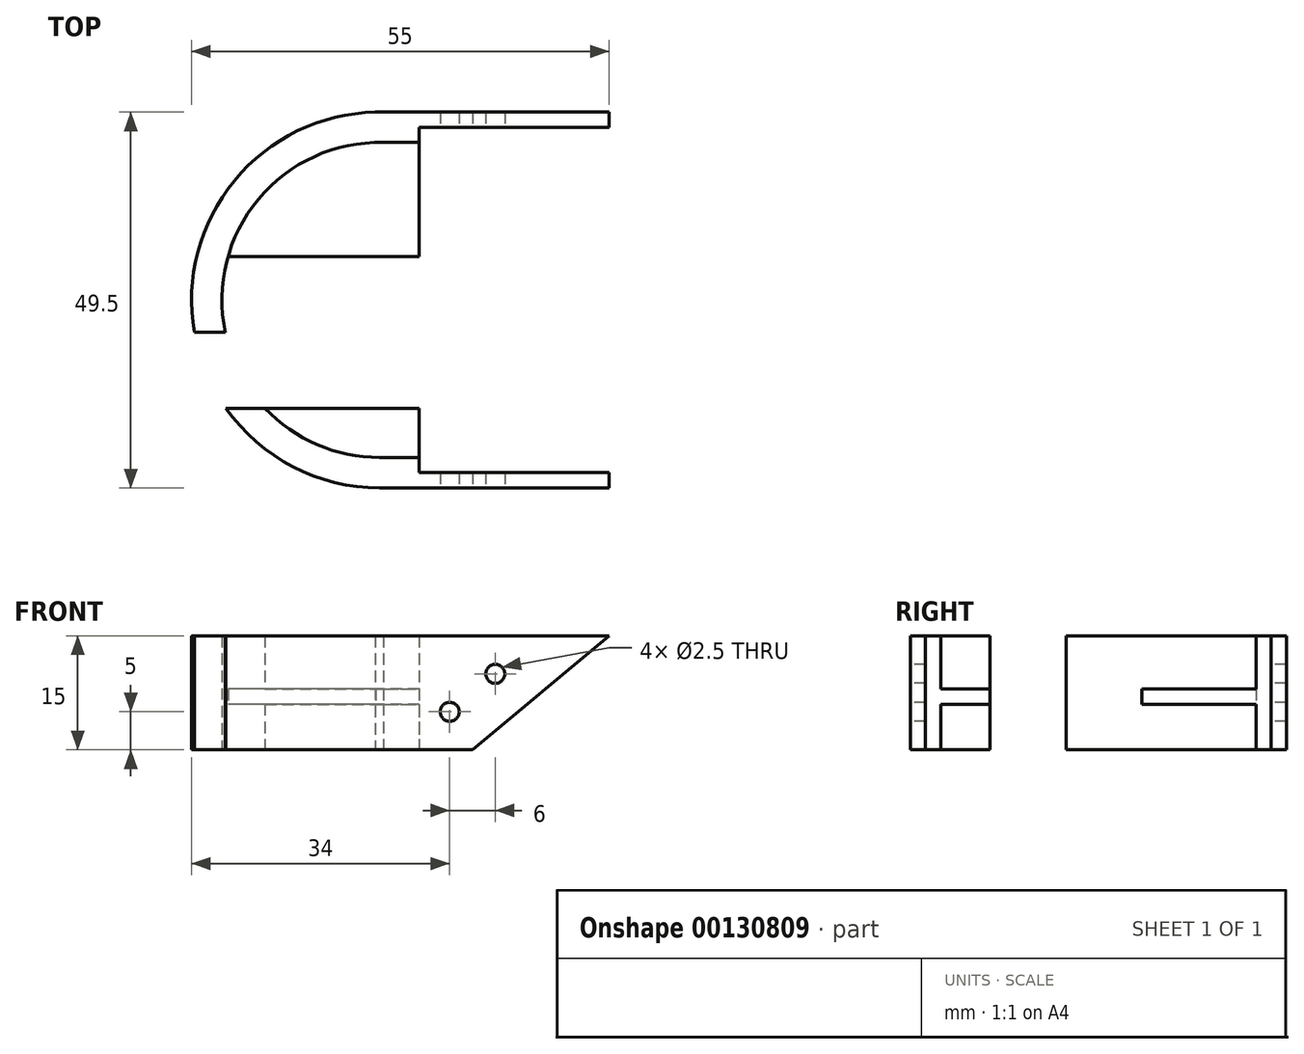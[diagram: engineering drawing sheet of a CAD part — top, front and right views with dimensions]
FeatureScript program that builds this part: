
annotation { "Feature Type Name" : "Feature", "Feature Type Description" : "" }
export const myFeature = defineFeature(function(context is Context, id is Id, definition is map)
    precondition{}
    {
        {
            var Q0;
            Q0=qCreatedBy(makeId("Top.planeOp"),FACE);
            var sketch = newSketch(context, id + "F0", { "sketchPlane" : qUnion([Q0])});
            skLineSegment(sketch, "E0.bottom", {"start": v(0, 0) * mm, "end": v(-30.79, 0) * mm});
            skLineSegment(sketch, "E0.top", {"start": v(0, -49.5) * mm, "end": v(-30.25, -49.5) * mm});
            skLineSegment(sketch, "E1.bottom", {"start": v(0, -2) * mm, "end": v(-25, -2) * mm});
            skLineSegment(sketch, "E1.top", {"start": v(0, -47.5) * mm, "end": v(-25, -47.5) * mm});
            skLineSegment(sketch, "E2.top", {"start": v(-29.75, -4) * mm, "end": v(-25, -4) * mm});
            skLineSegment(sketch, "E2.right", {"start": v(-25, -2) * mm, "end": v(-25, -4) * mm});
            skLineSegment(sketch, "E3.right", {"start": v(-25, -47.5) * mm, "end": v(-25, -45.5) * mm});
            skArc(sketch, "E4", {"start": v(-29.75, -4) * mm, "mid": v(-51, -24.5) * mm, "end": v(-30.25, -45.5) * mm});
            skArc(sketch, "E5", {"start": v(-30.79, 0) * mm, "mid": v(-55, -25.02) * mm, "end": v(-30.25, -49.5) * mm});
            skLineSegment(sketch, "E6.trimOffspring", {"start": v(-30.25, -45.5) * mm, "end": v(-25, -45.5) * mm});
            skLineSegment(sketch, "E7", {"start": v(0, -2) * mm, "end": v(0, 0) * mm});
            skLineSegment(sketch, "E8", {"start": v(0, -47.5) * mm, "end": v(0, -49.5) * mm});
            skSolve(sketch);
        }
        {
            var Q0;
            Q0=makeQuery(id+"F0.imprint","IMPRINT",FACE,{"disambiguationData":[TD([[makeQuery(id+"F0.imprint","IMPRINT",EDGE,{"derivedFrom":sQuery(id+"F0.wireOp",EDGE,"E0.bottom")}),1.0]])]});
            extrude(context, id + "F1", {"entities" : qUnion([Q0]), "depth" : 15 * mm});
        }
        {
            var Q0;
            Q0=qCreatedBy(makeId("Top.planeOp"),FACE);
            cPlane(context, id + "F2", {"entities" : qUnion([Q0]), "cplaneType" : CPlaneType.OFFSET, "offset" : 6 * mm, "width" : 150 * mm, "height" : 150 * mm});
        }
        {
            var Q0;
            Q0=qCreatedBy(id+"F2.planeOp",FACE);
            var sketch = newSketch(context, id + "F3", { "sketchPlane" : qUnion([Q0])});
            skLineSegment(sketch, "E9", {"start": v(-25, -39) * mm, "end": v(-25, -45.5) * mm});
            skLineSegment(sketch, "E10", {"start": v(-25, -45.5) * mm, "end": v(-43.74, -45.5) * mm});
            skLineSegment(sketch, "E11", {"start": v(-43.74, -45.5) * mm, "end": v(-50.48, -39) * mm});
            skLineSegment(sketch, "E12", {"start": v(-50.48, -39) * mm, "end": v(-25, -39) * mm});
            skLineSegment(sketch, "E13", {"start": v(-25, -4) * mm, "end": v(-25, -19) * mm});
            skLineSegment(sketch, "E14", {"start": v(-25, -19) * mm, "end": v(-54.32, -19) * mm});
            skLineSegment(sketch, "E15", {"start": v(-54.32, -19) * mm, "end": v(-43.75, -4) * mm});
            skLineSegment(sketch, "E16", {"start": v(-43.75, -4) * mm, "end": v(-25, -4) * mm});
            skSolve(sketch);
        }
        {
            var Q0;
            Q0=makeQuery(id+"F3.imprint","IMPRINT",FACE,{"disambiguationData":[TD([[makeQuery(id+"F3.imprint","IMPRINT",EDGE,{"derivedFrom":sQuery(id+"F3.wireOp",EDGE,"E9")}),-1.0]])]});
            var Q1;
            Q1=makeQuery(id+"F3.imprint","IMPRINT",FACE,{"disambiguationData":[TD([[makeQuery(id+"F3.imprint","IMPRINT",EDGE,{"derivedFrom":sQuery(id+"F3.wireOp",EDGE,"E13")}),-1.0]])]});
            extrude(context, id + "F4", {"entities" : qUnion([Q0, Q1]), "operationType" : NewBodyOperationType.ADD, "depth" : 2 * mm});
        }
        {
            var Q0;
            Q0=makeQuery(id+"F1.opExtrude","SWEPT_FACE",FACE,{"disambiguationData":[OSD([sQuery(id+"F0.wireOp",EDGE,"E0.bottom")])]});
            var sketch = newSketch(context, id + "F5", { "sketchPlane" : qUnion([Q0])});
            skLineSegment(sketch, "E17", {"start": v(18, 0) * mm, "end": v(0, 15) * mm});
            skLineSegment(sketch, "E18", {"start": v(0, 15) * mm, "end": v(0, 15) * mm});
            skLineSegment(sketch, "E19", {"start": v(0, 15) * mm, "end": v(0, 0) * mm});
            skLineSegment(sketch, "E20", {"start": v(0, 0) * mm, "end": v(18, 0) * mm});
            skCircle(sketch, "E21", {"center": v(21, 5) * mm, "radius": 1.25 * mm});
            skCircle(sketch, "E22", {"center": v(15, 10) * mm, "radius": 1.25 * mm});
            skSolve(sketch);
        }
        {
            var Q0;
            {var subQ0=sQuery(id+"F5.wireOp",EDGE,"E17");Q0=makeQuery(id+"F5.imprint","IMPRINT",FACE,{"disambiguationData":[TD([[makeQuery(id+"F5.imprint","IMPRINT",EDGE,{"derivedFrom":subQ0}),1.0]])]});}
            var Q1;
            Q1=makeQuery(id+"F5.imprint","IMPRINT",FACE,{"disambiguationData":[TD([[makeQuery(id+"F5.imprint","IMPRINT",EDGE,{"derivedFrom":sQuery(id+"F5.wireOp",EDGE,"E22")}),1.0]])]});
            var Q2;
            Q2=makeQuery(id+"F5.imprint","IMPRINT",FACE,{"disambiguationData":[TD([[makeQuery(id+"F5.imprint","IMPRINT",EDGE,{"derivedFrom":sQuery(id+"F5.wireOp",EDGE,"E21")}),1.0]])]});
            extrude(context, id + "F6", {"entities" : qUnion([Q0, Q1, Q2]), "operationType" : NewBodyOperationType.REMOVE, "endBound" : BoundingType.SYMMETRIC, "depth" : 600 * mm});
        }
        {
            var Q0;
            Q0=qCreatedBy(makeId("Right.planeOp"),FACE);
            var sketch = newSketch(context, id + "F7", { "sketchPlane" : qUnion([Q0])});
            skLineSegment(sketch, "E23", {"start": v(-39, 0) * mm, "end": v(-39, 15) * mm});
            skLineSegment(sketch, "E24", {"start": v(-39, 15) * mm, "end": v(-39, 15) * mm});
            skLineSegment(sketch, "E25", {"start": v(-29, 15) * mm, "end": v(-39, 15) * mm});
            skLineSegment(sketch, "E26", {"start": v(-29, 15) * mm, "end": v(-29, 0) * mm});
            skLineSegment(sketch, "E27", {"start": v(-29, 0) * mm, "end": v(-39, 0) * mm});
            skSolve(sketch);
        }
        {
            var Q0;
            Q0=qSketchRegion(id+"F7",true);
            extrude(context, id + "F8", {"entities" : qUnion([Q0]), "operationType" : NewBodyOperationType.REMOVE, "endBound" : BoundingType.THROUGH_ALL, "oppositeDirection" : true, "depth" : 25 * mm});
        }
    });
